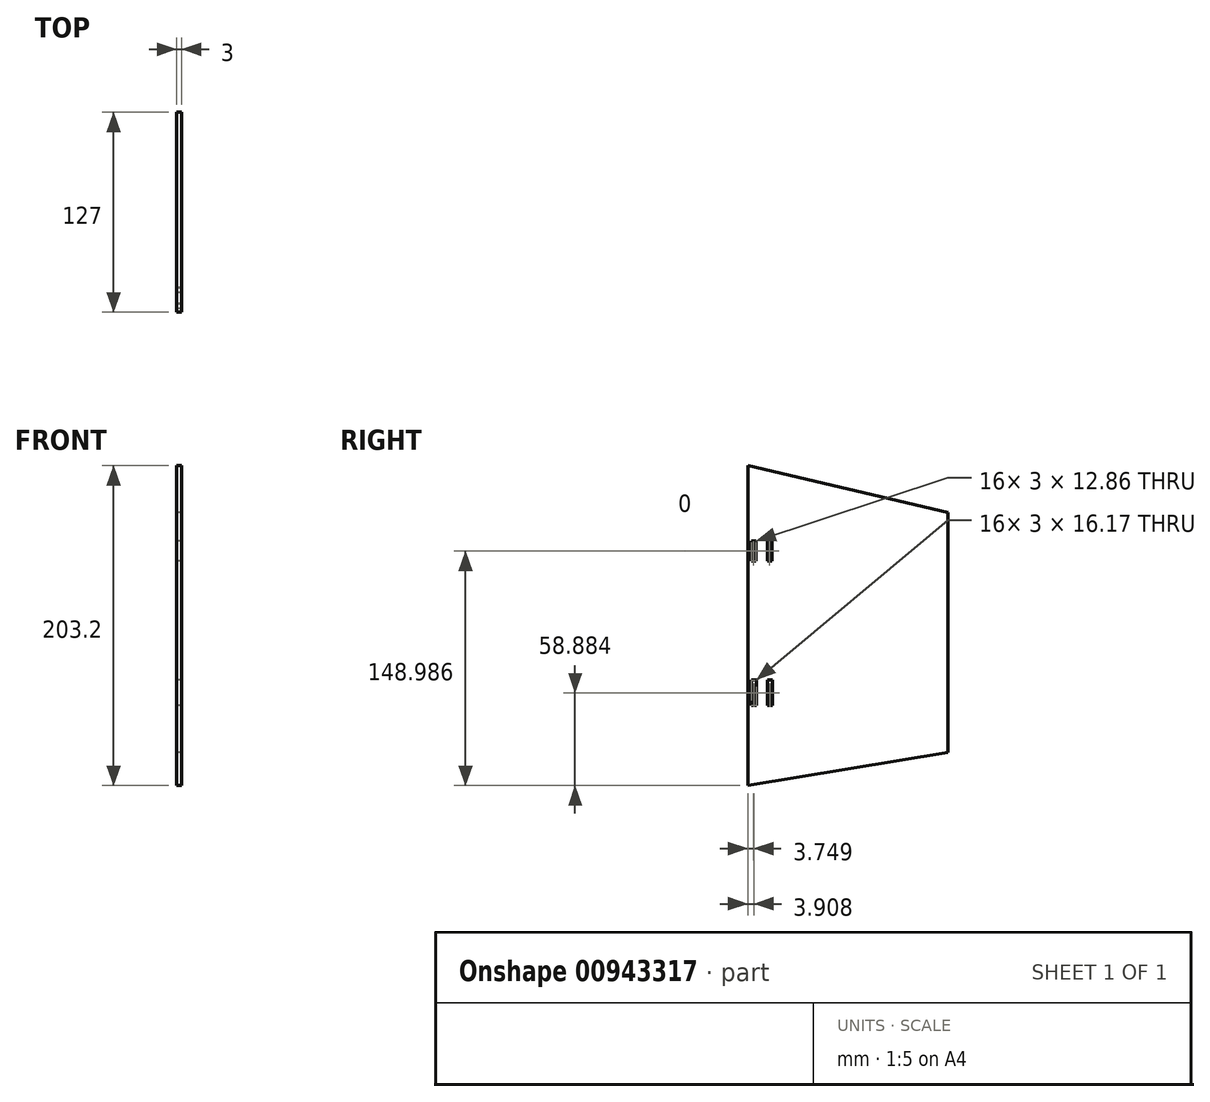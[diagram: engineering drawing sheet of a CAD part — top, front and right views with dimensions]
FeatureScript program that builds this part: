
annotation { "Feature Type Name" : "Feature", "Feature Type Description" : "" }
export const myFeature = defineFeature(function(context is Context, id is Id, definition is map)
    precondition{}
    {
        {
            var Q0;
            Q0=qCreatedBy(makeId("Right.planeOp"),FACE);
            var sketch = newSketch(context, id + "F0", { "sketchPlane" : qUnion([Q0])});
            skLineSegment(sketch, "E0.left", {"start": v(-25.74, 61.85) * mm, "end": v(-25.74, -141.35) * mm});
            skLineSegment(sketch, "E1.bottom", {"start": v(-23.5, 14.06) * mm, "end": v(-20.5, 14.06) * mm});
            skLineSegment(sketch, "E1.top", {"start": v(-23.5, 1.2) * mm, "end": v(-20.5, 1.2) * mm});
            skLineSegment(sketch, "E1.left", {"start": v(-23.5, 14.06) * mm, "end": v(-23.5, 1.2) * mm});
            skLineSegment(sketch, "E1.right", {"start": v(-20.5, 14.06) * mm, "end": v(-20.5, 1.2) * mm});
            skLineSegment(sketch, "E2.bottom", {"start": v(-23.33, -74.38) * mm, "end": v(-20.33, -74.38) * mm});
            skLineSegment(sketch, "E2.top", {"start": v(-23.33, -90.55) * mm, "end": v(-20.33, -90.55) * mm});
            skLineSegment(sketch, "E2.left", {"start": v(-23.33, -74.38) * mm, "end": v(-23.33, -90.55) * mm});
            skLineSegment(sketch, "E2.right", {"start": v(-20.33, -74.38) * mm, "end": v(-20.33, -90.55) * mm});
            skLineSegment(sketch, "E3.bottom", {"start": v(-13.35, 14.06) * mm, "end": v(-10.35, 14.06) * mm});
            skLineSegment(sketch, "E3.top", {"start": v(-13.35, 1.2) * mm, "end": v(-10.35, 1.2) * mm});
            skLineSegment(sketch, "E3.left", {"start": v(-13.35, 14.06) * mm, "end": v(-13.35, 1.2) * mm});
            skLineSegment(sketch, "E3.right", {"start": v(-10.35, 14.06) * mm, "end": v(-10.35, 1.2) * mm});
            skLineSegment(sketch, "E4.bottom", {"start": v(-10.19, -74.38) * mm, "end": v(-13.19, -74.38) * mm});
            skLineSegment(sketch, "E4.top", {"start": v(-10.19, -90.55) * mm, "end": v(-13.19, -90.55) * mm});
            skLineSegment(sketch, "E4.left", {"start": v(-10.19, -74.38) * mm, "end": v(-10.19, -90.55) * mm});
            skLineSegment(sketch, "E4.right", {"start": v(-13.19, -74.38) * mm, "end": v(-13.19, -90.55) * mm});
            skLineSegment(sketch, "E5", {"start": v(-25.74, -141.35) * mm, "end": v(101.26, -120.31) * mm});
            skLineSegment(sketch, "E6", {"start": v(101.26, -120.31) * mm, "end": v(101.26, 32.09) * mm});
            skLineSegment(sketch, "E7", {"start": v(101.26, 32.09) * mm, "end": v(-25.74, 61.85) * mm});
            skSolve(sketch);
        }
        {
            var Q0;
            Q0 = qSketchRegion(id + "F0", true);
            extrude(context, id + "F1", {"entities" : qUnion([Q0]), "depth" : 3 * mm, "offsetDistance" : 25.4 * mm});
        }
    });
